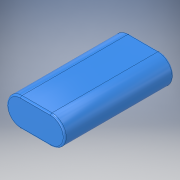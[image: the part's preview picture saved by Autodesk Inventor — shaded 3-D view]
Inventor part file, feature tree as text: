
AUTODESK INVENTOR PART (.ipt)
format: ipt  version: 2019 (Build 230136000, 136)  size: 129,024 bytes
history: native  units: mm
features: fillet x2, extrude x1, sketch x1
ambient origin geometry x8: Origin, YZ Plane, XZ Plane, XY Plane, X Axis, Y Axis, Z Axis, Center Point
bodies: Solid1 (feature_tree)
feature tree (4):
  extrude  "Extrusion1"  Depth=69.0mm
  fillet  "Fillet1"  Radius=18.0mm
  fillet  "Fillet2"  Radius=9.0mm
  sketch  "Sketch1"  dims[d0=37.0mm d1=69.0mm d2=18.0mm d3=0.0mm d4=9.0mm d5=1.0mm]
